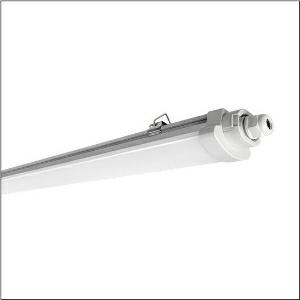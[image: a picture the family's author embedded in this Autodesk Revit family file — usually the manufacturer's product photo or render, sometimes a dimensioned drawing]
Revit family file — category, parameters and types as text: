
# Revit family: monsun_r__41_51fk20mn460a_a5b0
name_source: partatom
category: Lighting Fixtures
units: mm (PartAtom-declared; Revit-internal decimal feet)

## family parameters
Cut with Voids When Loaded = No
Host = Face
Light Source = No
Part Type = Normal
Room Calculation Point = No
Round Connector Dimension = Use Diameter
Shared = No

## types (1)
- --- (1 x LED, 6000 lm, 46 W, 4000K)
    Apparent Load = 46 VA
    CIE Flux Codes = 44 74 91 91 100
    Color Rendering = 80
    Color Temperature = 4000K
    Default Elevation = 1800 mm
    Description = Monsun® 41, damp-proof luminaire, primary optical cover: diffuser, of PC, frosted, light emission: direct distribution, primary light characteristic: symmetric, installation type: suspended mounting, surface-mounted, LED, rated luminous flux: 6.000lm, luminous efficacy: 130lm/W, light colour: 840, colour temperature: 4000K, control gear: ECG Multilumen, with terminal, 3-pole, mains connection: 220..240V, AC, 50/60Hz, rated input power: 46W, housing, luminaire housing, of PC, grey, length: 1.500mm, width: 79mm, height: 52mm, end cap, of PC, grey, ceiling mounting element, of stainless steel (V2A), protection rating (complete): IP65, insulation class (complete): insulation class II (safety insulation), certification: CE, UKCA, protection symbol: D, impact resistance: IK08, permissible operating ambient temperature: -20..+35°C, corresponds to IFS (International Featured Standards) requirements for safety and quality in the food industry, packaging unit: 1 piece
    Height = 54 mm
    Lamp = 1 x LED
    Lamp Light Flux = 6000 lm
    Lamp Power = 46 W
    Lamp count = 1
    Length = 1500 mm
    Luminous efficacy = 130 lm/W
    Manufacturer = Siteco
    ModVariant = No
    Model = 51FK20MN460A
    Mounting Place = Ceiling
    Mounting Type = Surface mounted
    Number of Poles = 1
    OnlyDefault = Yes
    Power Factor = 1
    Product Name = Monsun® 41
    Product group = damp-proof luminaire | ceiling mounted
    ProductGroupID = 300
    Protection Class = Protection class II
    Protection Degree = IP 65
    RLX_Detail_Level = 1
    RlxData = <blob elided: 28717 chars, md5=a3a16fc9>
    Socket = socket
    Standby Power = 0 W
    System Light Flux = 6000 lm
    System Power = 46 W
    Type Comments = factory setting: luminous flux: 100 % | (HIGH)
    Type Image = l_1007037.jpg
    URL = http://relux.com
    VarID = @adj_087099
    Voltage = 0 V
    Weight = 0.00 kg
    Width = 79 mm

## geometry (parser evidence)
native form markers: Blend x4, Sweep x11
no freeform markers — native parametric forms only
